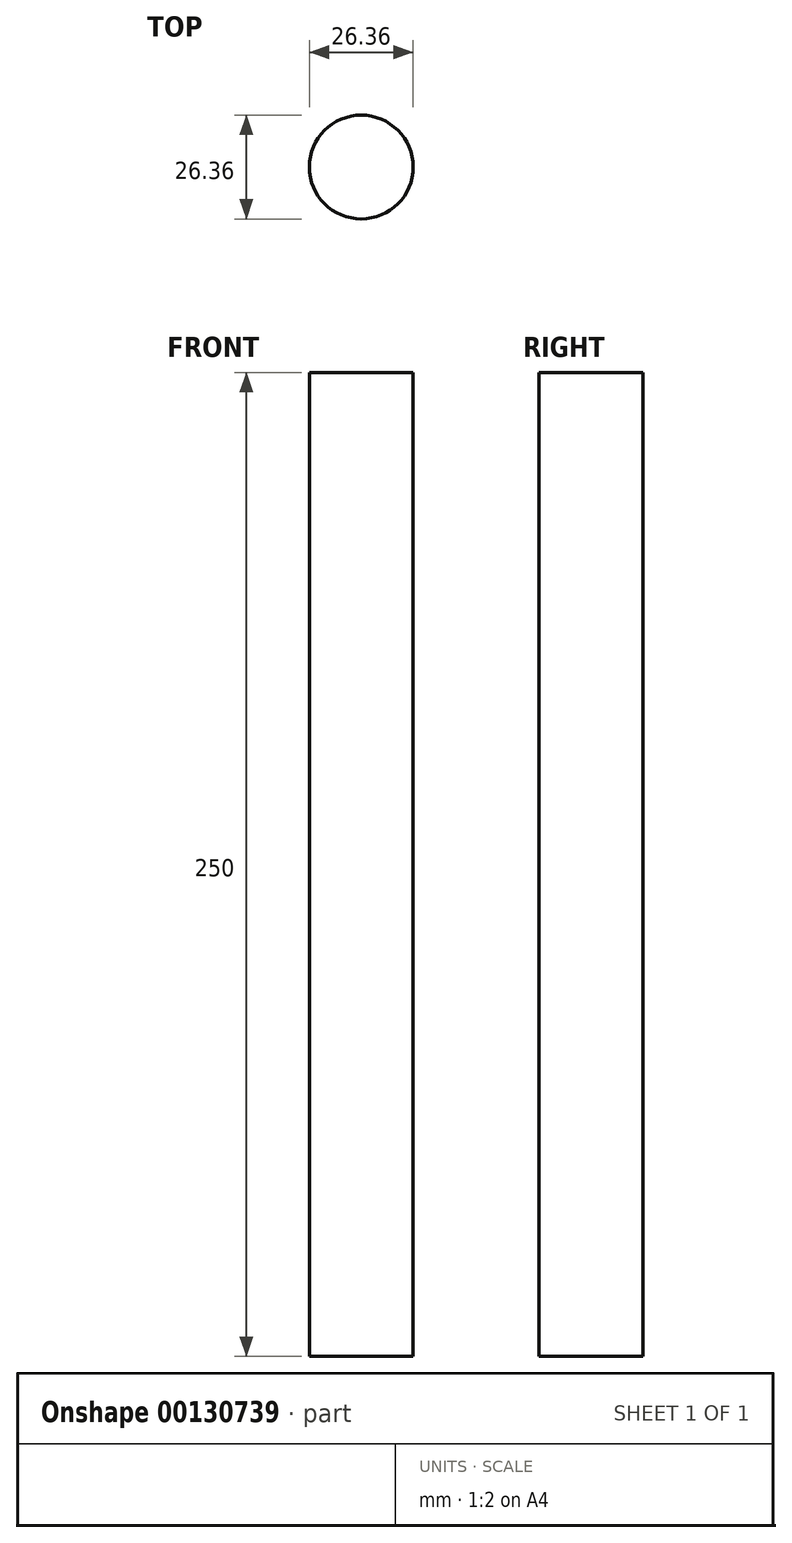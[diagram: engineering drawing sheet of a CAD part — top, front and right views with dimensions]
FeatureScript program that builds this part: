
annotation { "Feature Type Name" : "Feature", "Feature Type Description" : "" }
export const myFeature = defineFeature(function(context is Context, id is Id, definition is map)
    precondition{}
    {
        {
            var Q0;
            Q0=qCreatedBy(makeId("Top.planeOp"),FACE);
            var sketch = newSketch(context, id + "F0", { "sketchPlane" : qUnion([Q0])});
            skCircle(sketch, "E0", {"center": v(0, 0) * mm, "radius": 13.18 * mm});
            skSolve(sketch);
        }
        {
            var Q0;
            Q0=sQuery(id+"F0.wireOp",EDGE,"E0");
            extrude(context, id + "F1", {"bodyType" : ToolBodyType.SURFACE, "surfaceEntities" : qUnion([Q0]), "depth" : 250 * mm});
        }
    });
